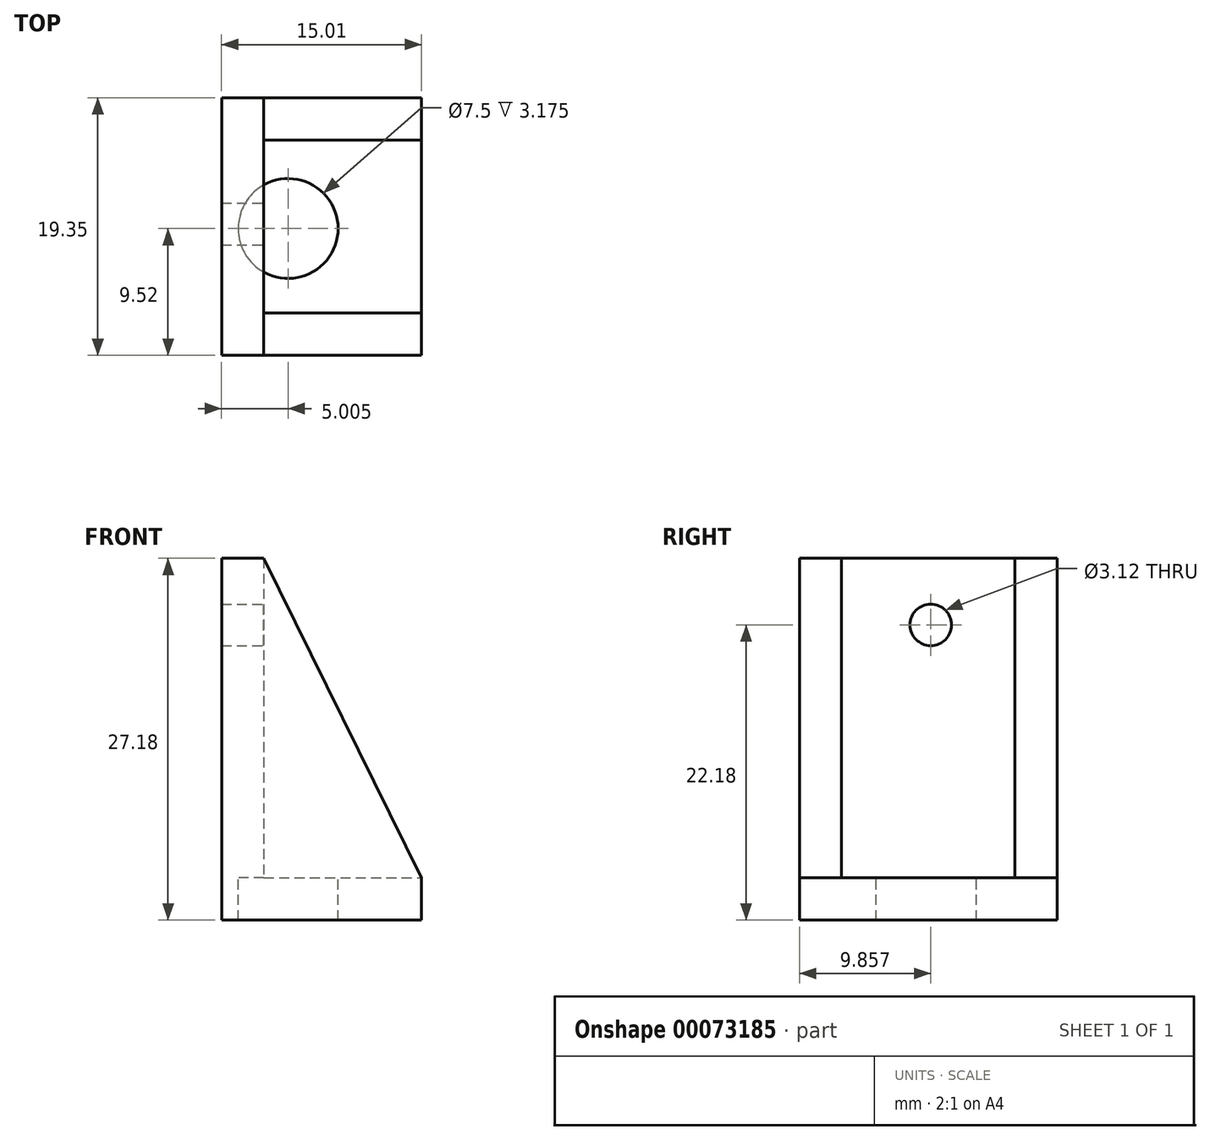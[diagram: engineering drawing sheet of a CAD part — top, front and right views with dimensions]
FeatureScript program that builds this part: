
annotation { "Feature Type Name" : "Feature", "Feature Type Description" : "" }
export const myFeature = defineFeature(function(context is Context, id is Id, definition is map)
    precondition{}
    {
        {
            var Q0;
            Q0=qCreatedBy(makeId("Front.planeOp"),FACE);
            var sketch = newSketch(context, id + "F0", { "sketchPlane" : qUnion([Q0])});
            skLineSegment(sketch, "E0", {"start": v(-3.17, 24) * mm, "end": v(0, 24) * mm});
            skLineSegment(sketch, "E1", {"start": v(0, 24) * mm, "end": v(0, 0) * mm});
            skLineSegment(sketch, "E2", {"start": v(0, 0) * mm, "end": v(11.82, 0) * mm});
            skLineSegment(sketch, "E3", {"start": v(11.83, 0) * mm, "end": v(11.83, -3.18) * mm});
            skLineSegment(sketch, "E4", {"start": v(11.83, -3.17) * mm, "end": v(-3.17, -3.18) * mm});
            skLineSegment(sketch, "E5", {"start": v(-3.17, -3.17) * mm, "end": v(-3.17, 24) * mm});
            skSolve(sketch);
        }
        {
            var Q0;
            Q0 = qSketchRegion(id + "F0", true);
            extrude(context, id + "F1", {"entities" : qUnion([Q0]), "depth" : 13 * mm});
        }
        {
            var Q0;
            Q0=makeQuery(id+"F1.opExtrude","CAP_FACE",FACE,{"disambiguationData":[OSD([sQuery(id+"F0.wireOp",EDGE,"E0"),sQuery(id+"F0.wireOp",EDGE,"E1"),sQuery(id+"F0.wireOp",EDGE,"E2"),sQuery(id+"F0.wireOp",EDGE,"E3"),sQuery(id+"F0.wireOp",EDGE,"E4"),sQuery(id+"F0.wireOp",EDGE,"E5")])],"isStart":false});
            var sketch = newSketch(context, id + "F2", { "sketchPlane" : qUnion([Q0])});
            skLineSegment(sketch, "E6", {"start": v(-3.17, 24) * mm, "end": v(-3.17, -3.17) * mm});
            skLineSegment(sketch, "E7", {"start": v(-3.17, -3.17) * mm, "end": v(11.83, -3.17) * mm});
            skLineSegment(sketch, "E8", {"start": v(11.83, -3.17) * mm, "end": v(11.83, 0) * mm});
            skLineSegment(sketch, "E9", {"start": v(11.83, 0) * mm, "end": v(0, 24) * mm});
            skLineSegment(sketch, "E10", {"start": v(0, 24) * mm, "end": v(-3.17, 24) * mm});
            skSolve(sketch);
        }
        {
            var Q0;
            Q0 = qSketchRegion(id + "F2", true);
            extrude(context, id + "F3", {"entities" : qUnion([Q0]), "operationType" : NewBodyOperationType.ADD, "depth" : 3.17 * mm});
        }
        {
            var Q0;
            Q0=makeQuery(id+"F1.opExtrude","CAP_FACE",FACE,{"disambiguationData":[OSD([sQuery(id+"F0.wireOp",EDGE,"E0"),sQuery(id+"F0.wireOp",EDGE,"E1"),sQuery(id+"F0.wireOp",EDGE,"E2"),sQuery(id+"F0.wireOp",EDGE,"E3"),sQuery(id+"F0.wireOp",EDGE,"E4"),sQuery(id+"F0.wireOp",EDGE,"E5")])],"isStart":true});
            var sketch = newSketch(context, id + "F4", { "sketchPlane" : qUnion([Q0])});
            skLineSegment(sketch, "E11", {"start": v(3.17, 24) * mm, "end": v(0, 24) * mm});
            skLineSegment(sketch, "E12", {"start": v(0, 24) * mm, "end": v(-11.82, 0) * mm});
            skLineSegment(sketch, "E13", {"start": v(-11.82, 0) * mm, "end": v(-11.83, -3.18) * mm});
            skLineSegment(sketch, "E14", {"start": v(-11.83, -3.18) * mm, "end": v(3.17, -3.18) * mm});
            skLineSegment(sketch, "E15", {"start": v(3.17, -3.17) * mm, "end": v(3.17, 24) * mm});
            skSolve(sketch);
        }
        {
            var Q0;
            Q0 = qSketchRegion(id + "F4", true);
            extrude(context, id + "F5", {"entities" : qUnion([Q0]), "operationType" : NewBodyOperationType.ADD, "depth" : 3.17 * mm});
        }
        {
            var Q0;
            Q0=makeQuery(id+"F1.opExtrude","SWEPT_FACE",FACE,{"disambiguationData":[OSD([sQuery(id+"F0.wireOp",EDGE,"E2")])]});
            var sketch = newSketch(context, id + "F6", { "sketchPlane" : qUnion([Q0])});
            skCircle(sketch, "E16", {"center": v(1.82, -6.65) * mm, "radius": 3.75 * mm});
            skSolve(sketch);
        }
        {
            var Q0;
            Q0 = qSketchRegion(id + "F6", true);
            extrude(context, id + "F7", {"entities" : qUnion([Q0]), "operationType" : NewBodyOperationType.REMOVE, "endBound" : BoundingType.THROUGH_ALL, "oppositeDirection" : true, "depth" : 25 * mm});
        }
        {
            var Q0;
            Q0=makeQuery(id+"F1.opExtrude","SWEPT_FACE",FACE,{"disambiguationData":[OSD([sQuery(id+"F0.wireOp",EDGE,"E1")])]});
            var sketch = newSketch(context, id + "F8", { "sketchPlane" : qUnion([Q0])});
            skCircle(sketch, "E17", {"center": v(-6.31, 19) * mm, "radius": 1.56 * mm});
            skSolve(sketch);
        }
        {
            var Q0;
            Q0 = qSketchRegion(id + "F8", true);
            extrude(context, id + "F9", {"entities" : qUnion([Q0]), "operationType" : NewBodyOperationType.REMOVE, "endBound" : BoundingType.THROUGH_ALL, "oppositeDirection" : true, "depth" : 25 * mm});
        }
    });
